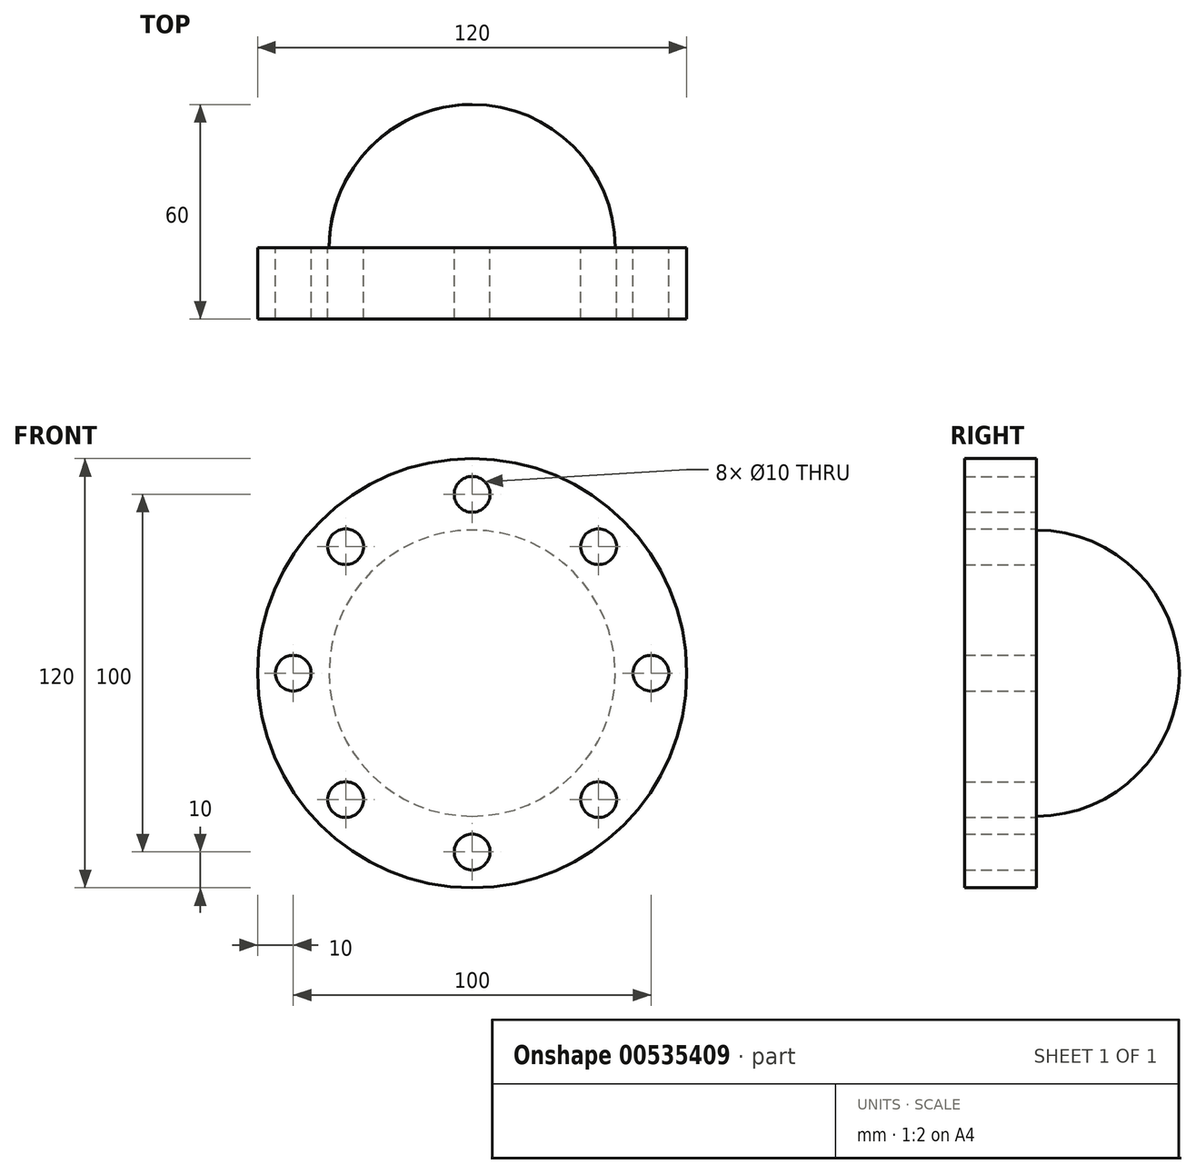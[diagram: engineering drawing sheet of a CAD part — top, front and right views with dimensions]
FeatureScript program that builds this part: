
annotation { "Feature Type Name" : "Feature", "Feature Type Description" : "" }
export const myFeature = defineFeature(function(context is Context, id is Id, definition is map)
    precondition{}
    {
        {
            var Q0;
            Q0=qCreatedBy(makeId("Front.planeOp"),FACE);
            var sketch = newSketch(context, id + "F0", { "sketchPlane" : qUnion([Q0])});
            skCircle(sketch, "E0", {"center": v(0, 0) * mm, "radius": 60 * mm});
            skCircle(sketch, "E1", {"center": v(0, 50) * mm, "radius": 5 * mm});
            skCircle(sketch, "E2.1.0", {"center": v(-35.36, 35.36) * mm, "radius": 5 * mm});
            skCircle(sketch, "E2.2.0", {"center": v(-50, 0) * mm, "radius": 5 * mm});
            skCircle(sketch, "E2.3.0", {"center": v(-35.36, -35.36) * mm, "radius": 5 * mm});
            skCircle(sketch, "E2.4.0", {"center": v(0, -50) * mm, "radius": 5 * mm});
            skCircle(sketch, "E2.5.0", {"center": v(35.36, -35.36) * mm, "radius": 5 * mm});
            skCircle(sketch, "E2.6.0", {"center": v(50, 0) * mm, "radius": 5 * mm});
            skCircle(sketch, "E2.7.0", {"center": v(35.36, 35.36) * mm, "radius": 5 * mm});
            skSolve(sketch);
        }
        {
            var Q0;
            Q0=makeQuery(id+"F0.imprint","IMPRINT",FACE,{"disambiguationData":[TD([[makeQuery(id+"F0.imprint","IMPRINT",EDGE,{"derivedFrom":sQuery(id+"F0.wireOp",EDGE,"E0")}),1.0]])]});
            extrude(context, id + "F1", {"entities" : qUnion([Q0]), "depth" : 20 * mm, "offsetDistance" : 25 * mm});
        }
        {
            var Q0;
            Q0=qCreatedBy(makeId("Top.planeOp"),FACE);
            var sketch = newSketch(context, id + "F2", { "sketchPlane" : qUnion([Q0])});
            skLineSegment(sketch, "E3", {"start": v(60, 0) * mm, "end": v(60, -20) * mm});
            skLineSegment(sketch, "E4", {"start": v(-60, -20) * mm, "end": v(-60, 0) * mm});
            skArc(sketch, "E5", {"start": v(0, 40) * mm, "mid": v(-28.28, 28.28) * mm, "end": v(-40, 0) * mm});
            skLineSegment(sketch, "E6", {"start": v(0, 40) * mm, "end": v(0, 0) * mm});
            skLineSegment(sketch, "E7.0", {"start": v(60, -20) * mm, "end": v(-60, -20) * mm});
            skLineSegment(sketch, "E8.0", {"start": v(0, 0) * mm, "end": v(-40, 0) * mm});
            skPoint(sketch, "E9.orphan", {"position": v(-60, 0) * mm});
            skPoint(sketch, "E10.orphan", {"position": v(60, 0) * mm});
            skSolve(sketch);
        }
        {
            var Q0;
            Q0 = qSketchRegion(id + "F2", true);
            var Q1;
            Q1=sQuery(id+"F2.wireOp",EDGE,"E6");
            revolve(context, id + "F3", {"operationType" : NewBodyOperationType.ADD, "entities" : qUnion([Q0]), "axis" : qUnion([Q1]), "revolveType" : RevolveType.FULL, "oppositeDirection" : true});
        }
    });
